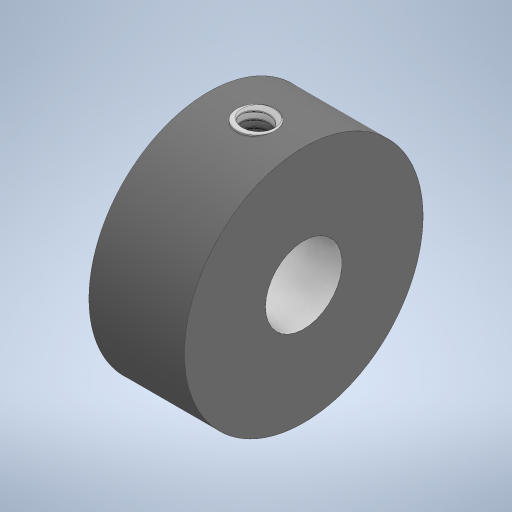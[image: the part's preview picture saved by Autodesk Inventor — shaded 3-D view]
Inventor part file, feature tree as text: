
AUTODESK INVENTOR PART (.ipt)
format: ipt  version: 2023 (Build 270158000, 158)  size: 728,576 bytes
history: native  units: in
note: dims shown in document units (in); Inventor stores cm internally (conversion verified against a paired STEP export)
features: sketch x5, extrude x3, plane x1, thread x1, revolve x1, helix x1
ambient origin geometry x8: Origin, YZ Plane, XZ Plane, XY Plane, X Axis, Y Axis, Z Axis, Center Point
bodies: Solid1 (feature_tree), Solid4 (feature_tree)
feature tree (12):
  extrude  "Extrusion1"  Depth=0.3937in TaperAngle=0.0deg
  plane  "Work Plane1"
  sketch  "Sketch2"  dims[d3=0.4921in d4=0.1575in]
  extrude  "Extrusion2"  Depth=0.1575in
  extrude  "Extrusion3"  Depth=0.3937in TaperAngle=0.0deg
  thread  "Thread3"  [1 undecoded]
  revolve  "Revolution3"  [1 undecoded]
  helix  "Coil3"  [1 undecoded]
  sketch  "Sketch1"  dims[d0=0.9843in d1=0.3937in d2=0.0in]
  sketch  "Sketch5"  dims[d5=0.1969in d6=0.3937in d7=0.0in d17=0.3779in]
  sketch  "Sketch8"  dims[d28=0.315in d29=0.3937in d30=0.0in d40=0.3779in]
  sketch  "Sketch9"  dims[d51=0.315in d52=0.0in d53=0.3779in d54=0.0047in d55=0.0047in d58=0.0295in d60=0.3779in d62=0.0in d63=0.0296in d64=0.374in d65=0.3937in d66=0.0in d67=0.0in d68=0.0in d69=0.0in d70=0.0in]
note: 3 required parameter values undecoded (feature->parameter linkage not recoverable at this tier; creation-order binding heuristic only, values carry confidence <= 0.55)